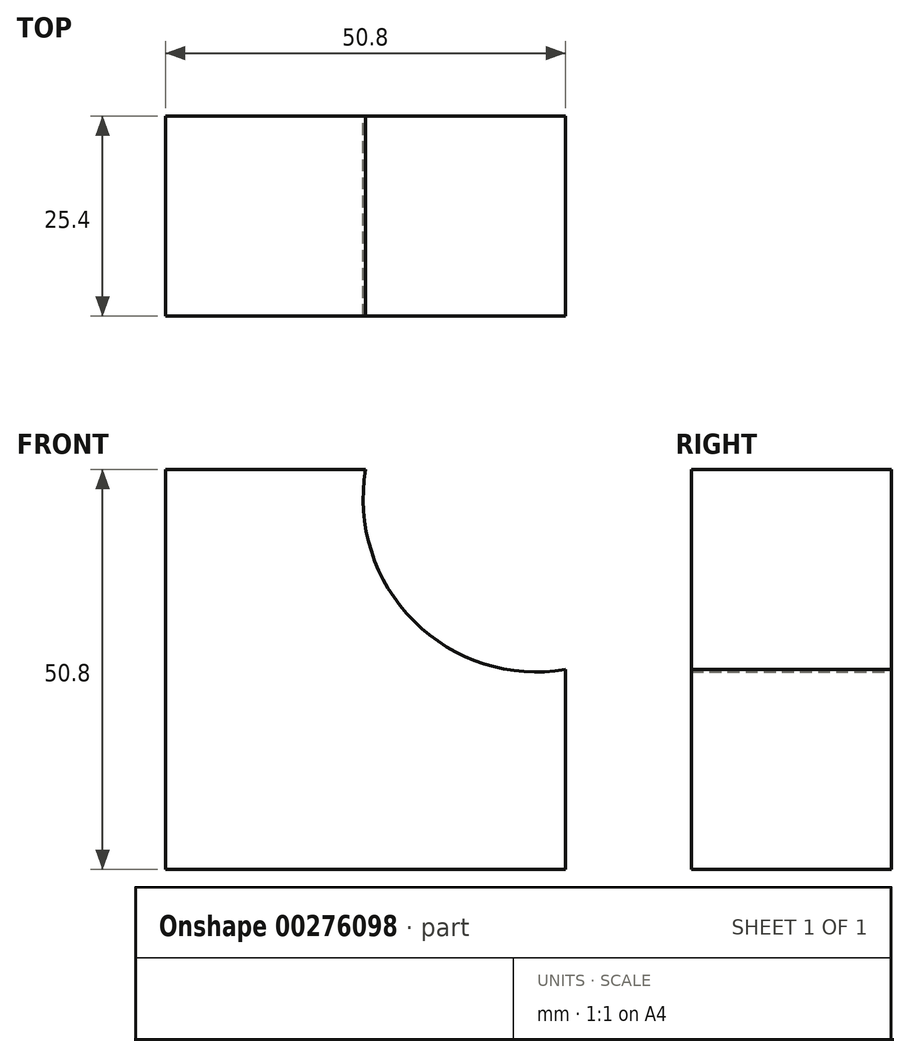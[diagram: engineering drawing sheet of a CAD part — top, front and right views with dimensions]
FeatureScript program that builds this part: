
annotation { "Feature Type Name" : "Feature", "Feature Type Description" : "" }
export const myFeature = defineFeature(function(context is Context, id is Id, definition is map)
    precondition{}
    {
        {
            var Q0;
            Q0=qCreatedBy(makeId("Front.planeOp"),FACE);
            var sketch = newSketch(context, id + "F0", { "sketchPlane" : qUnion([Q0])});
            skLineSegment(sketch, "E0", {"start": v(-57.29, 50.8) * mm, "end": v(-57.29, 0) * mm});
            skLineSegment(sketch, "E1", {"start": v(-57.29, 0) * mm, "end": v(-6.49, 0) * mm});
            skLineSegment(sketch, "E2", {"start": v(-6.49, 0) * mm, "end": v(-6.49, 25.4) * mm});
            skLineSegment(sketch, "E3", {"start": v(-31.89, 50.8) * mm, "end": v(-57.29, 50.8) * mm});
            skArc(sketch, "E4", {"start": v(-31.89, 50.8) * mm, "mid": v(-25.75, 31.54) * mm, "end": v(-6.49, 25.4) * mm});
            skSolve(sketch);
        }
        {
            var Q0;
            Q0 = qSketchRegion(id + "F0", true);
            extrude(context, id + "F1", {"entities" : qUnion([Q0]), "depth" : 25.4 * mm});
        }
    });
